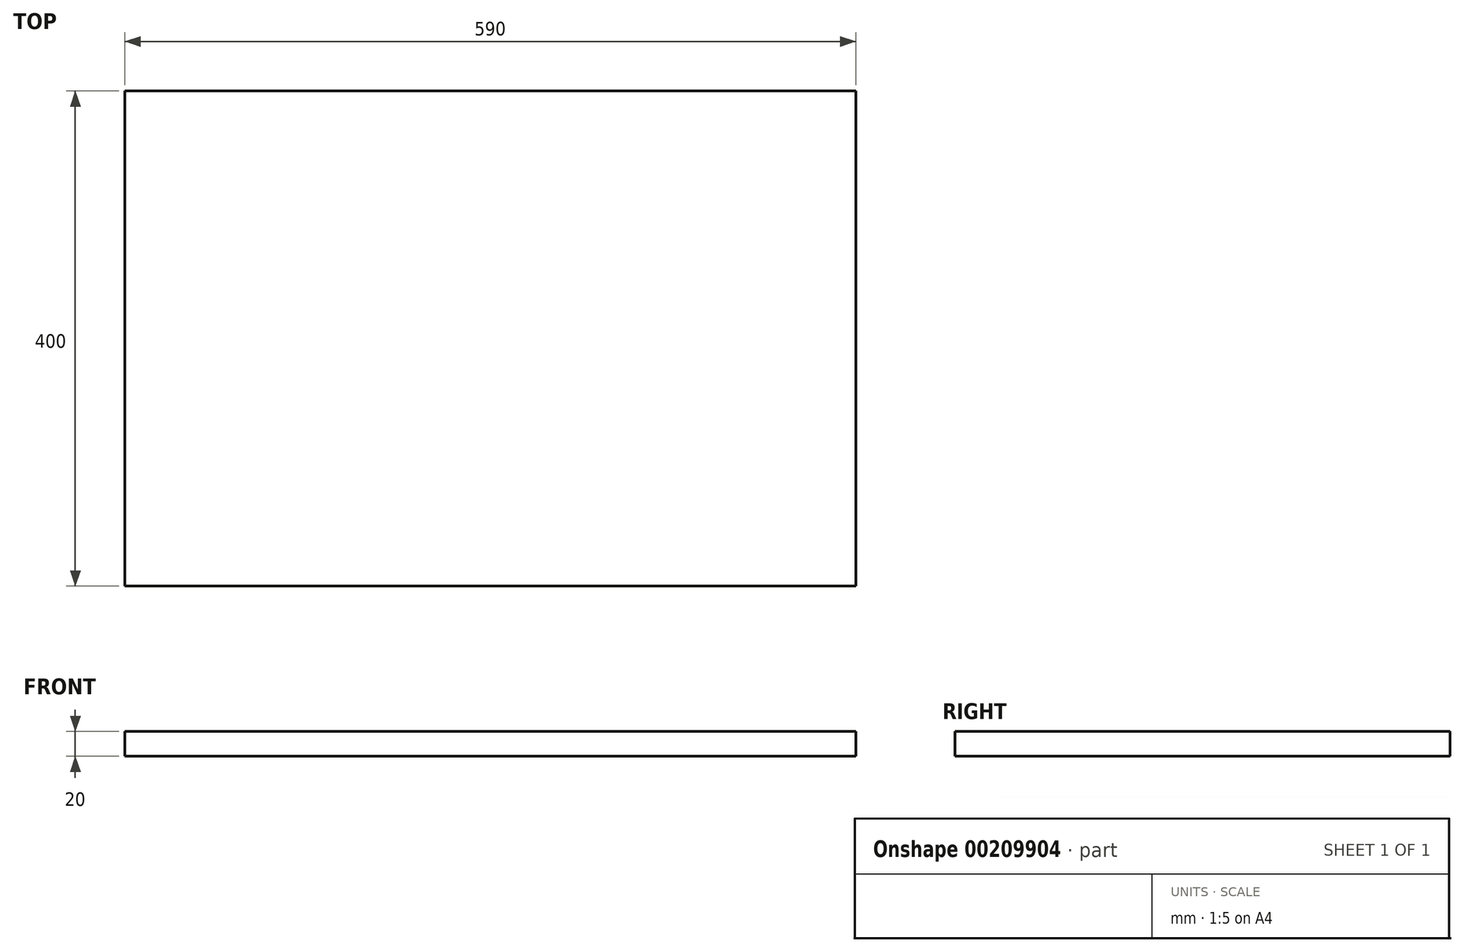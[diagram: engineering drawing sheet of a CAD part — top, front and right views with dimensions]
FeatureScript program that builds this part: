
annotation { "Feature Type Name" : "Feature", "Feature Type Description" : "" }
export const myFeature = defineFeature(function(context is Context, id is Id, definition is map)
    precondition{}
    {
        {
            var Q0;
            Q0=qCreatedBy(makeId("Top.planeOp"),FACE);
            var sketch = newSketch(context, id + "F0", { "sketchPlane" : qUnion([Q0])});
            skLineSegment(sketch, "E0.bottom", {"start": v(-295, 200) * mm, "end": v(295, 200) * mm});
            skLineSegment(sketch, "E0.top", {"start": v(-295, -200) * mm, "end": v(295, -200) * mm});
            skLineSegment(sketch, "E0.left", {"start": v(-295, 200) * mm, "end": v(-295, -200) * mm});
            skLineSegment(sketch, "E0.right", {"start": v(295, 200) * mm, "end": v(295, -200) * mm});
            skPoint(sketch, "E0.middle", {"position": v(0, 0) * mm});
            skSolve(sketch);
        }
        {
            var Q0;
            Q0=makeQuery(id+"F0.imprint","IMPRINT",FACE,{"disambiguationData":[TD([[makeQuery(id+"F0.imprint","IMPRINT",EDGE,{"derivedFrom":sQuery(id+"F0.wireOp",EDGE,"E0.bottom")}),-1.0]])]});
            extrude(context, id + "F1", {"entities" : qUnion([Q0]), "depth" : 20 * mm});
        }
    });
